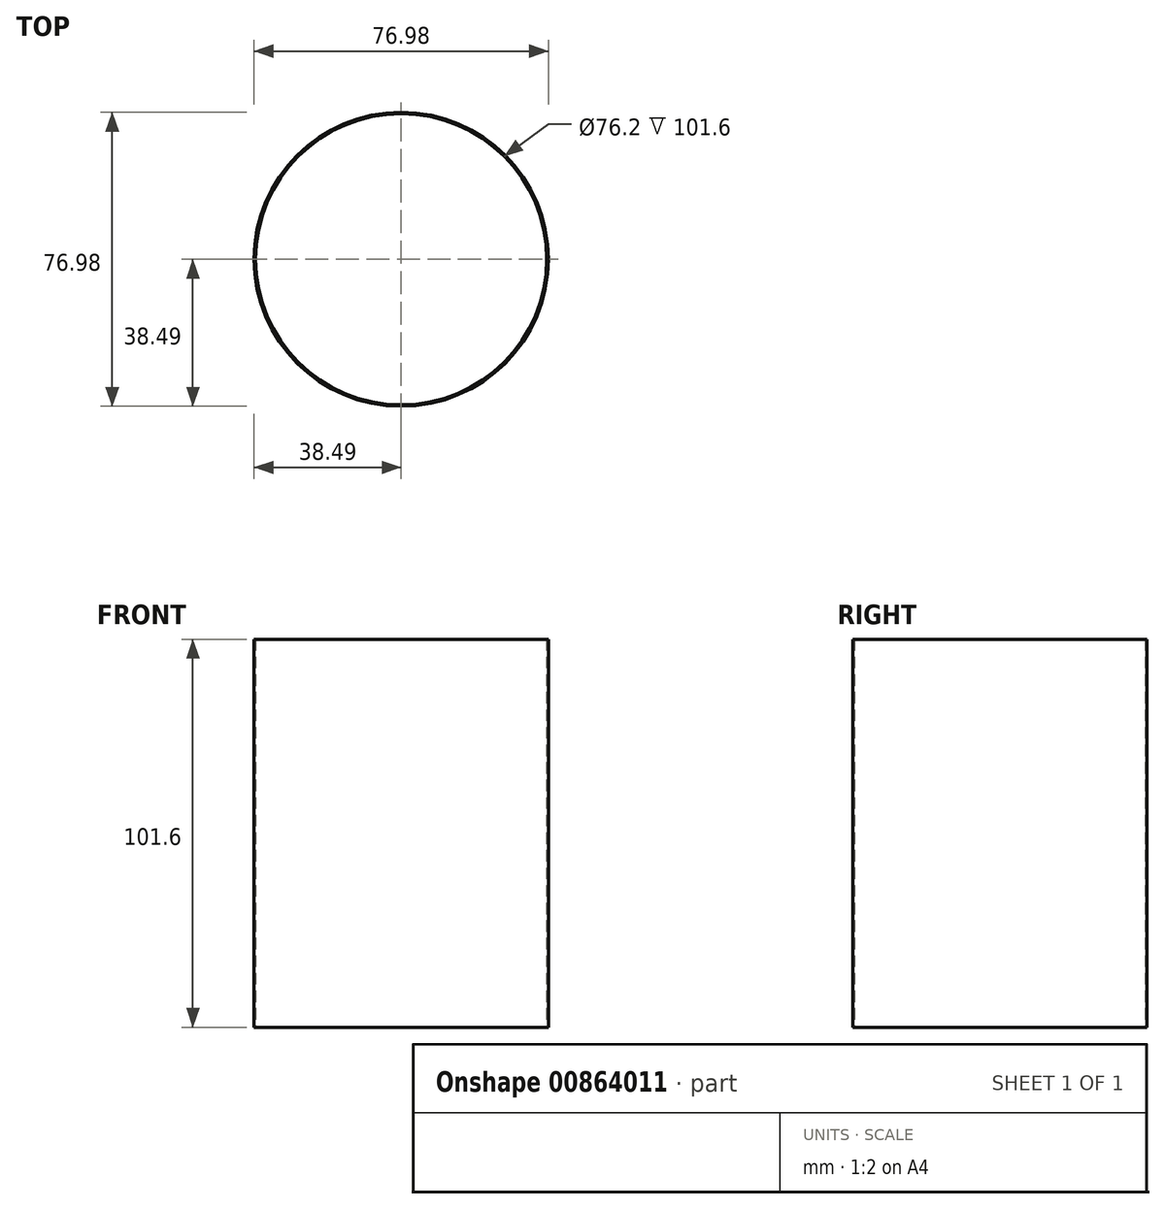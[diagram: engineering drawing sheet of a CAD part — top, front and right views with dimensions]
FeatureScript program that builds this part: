
annotation { "Feature Type Name" : "Feature", "Feature Type Description" : "" }
export const myFeature = defineFeature(function(context is Context, id is Id, definition is map)
    precondition{}
    {
        {
            var Q0;
            Q0=qCreatedBy(makeId("Top.planeOp"),FACE);
            var sketch = newSketch(context, id + "F0", { "sketchPlane" : qUnion([Q0])});
            skCircle(sketch, "E0", {"center": v(0, 0) * mm, "radius": 38.1 * mm});
            skCircle(sketch, "E1", {"center": v(0, 0) * mm, "radius": 38.5 * mm});
            skSolve(sketch);
        }
        {
            var Q0;
            Q0 = qSketchRegion(id + "F0", true);
            extrude(context, id + "F1", {"entities" : qUnion([Q0]), "depth" : 101.6 * mm, "offsetDistance" : 25.4 * mm});
        }
    });
